# Revit family: Haworth_Maari_Chair_StarBase_wTablet_AP_PRELIMINARY
name_source: partatom
category: Furniture
units: mm (PartAtom-declared; Revit-internal decimal feet)

## family parameters
Always vertical = Yes
Cut with Voids When Loaded = No
OmniClass Number = 23.40.70.14.64.21
OmniClass Title = Systems Furniture
Room Calculation Point = No
Shared = No
Work Plane-Based = No

## types (2) — shared parameters
Actual Depth = 724 mm
Actual Height = 813 mm
Actual Width = 724 mm
Arm Cap Finish = Haworth _ Polymer _ Undecided
Assembly Code = E2020200
Description = Haworth - Maari - Chair - Star Base - with Tablet
Manufacturer = Haworth
Model = SEMIGX
Revision Number = 2
Seat Pan Finish = Haworth _ Paint _ Black
Size = Verify Final Dim. w/ Haworth
URL = https://www.haworth.com
URL - Product = https://www.haworth.com
Warranty = http://www.haworth.com

## per-type parameters (varying)
| type | With Arms |
| Five Star Base - With Arms | Yes |
| Five Star Base - No Arms | No |

## geometry (parser evidence)
native form markers: Sweep x14
no freeform markers — native parametric forms only
